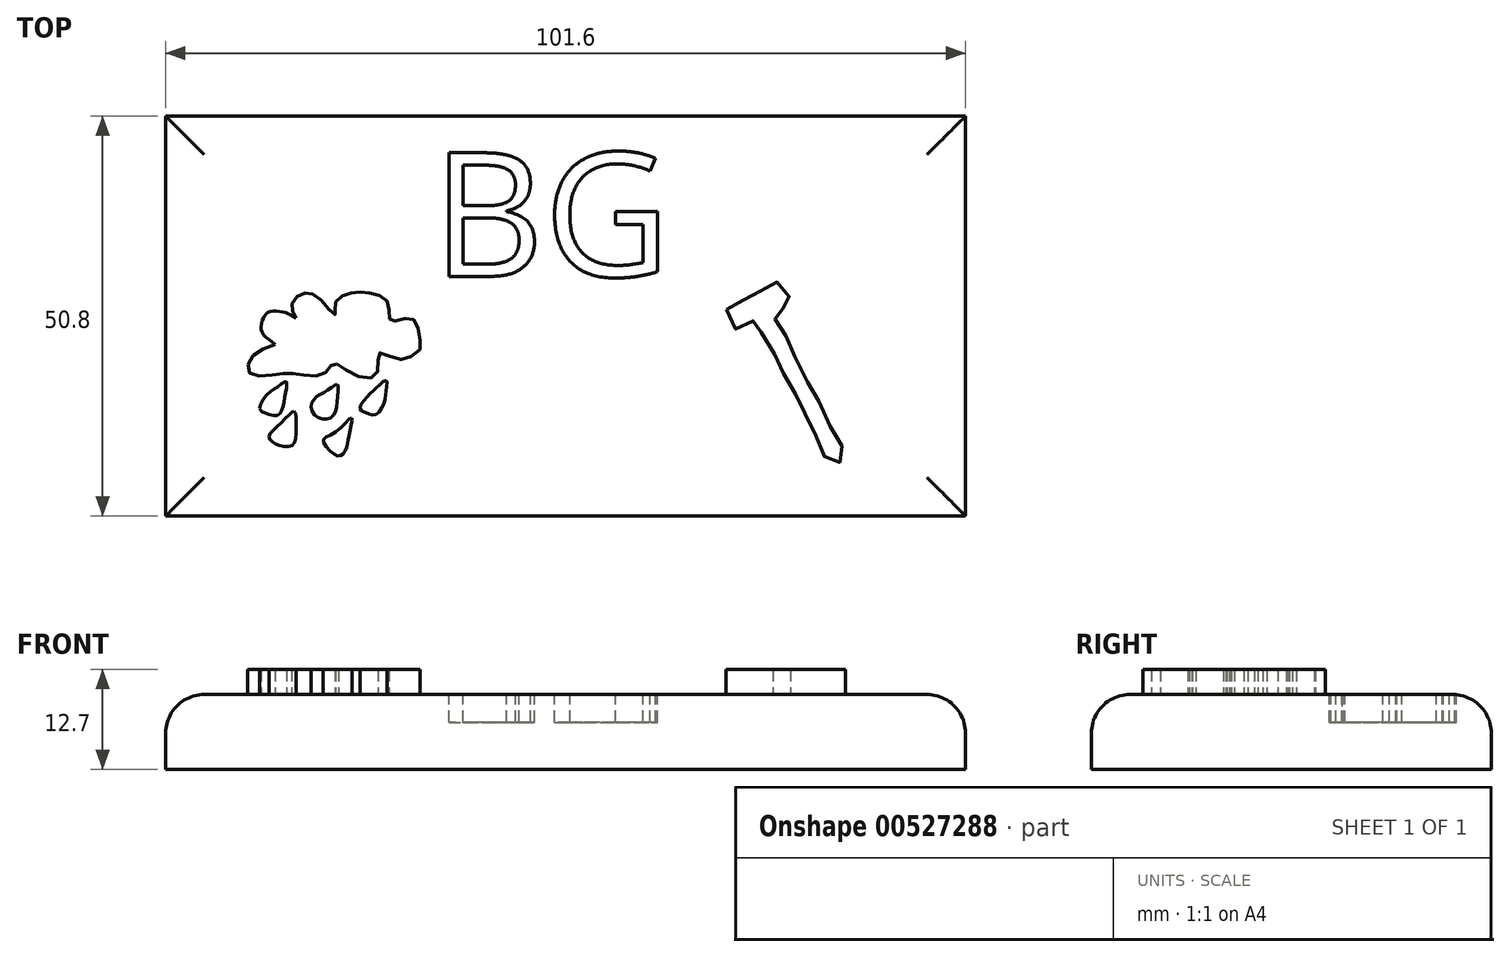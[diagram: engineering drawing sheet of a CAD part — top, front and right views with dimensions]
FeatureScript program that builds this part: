
annotation { "Feature Type Name" : "Feature", "Feature Type Description" : "" }
export const myFeature = defineFeature(function(context is Context, id is Id, definition is map)
    precondition{}
    {
        {
            var Q0;
            Q0=qCreatedBy(makeId("Top.planeOp"),FACE);
            var sketch = newSketch(context, id + "F0", { "sketchPlane" : qUnion([Q0])});
            skLineSegment(sketch, "E0.bottom", {"start": v(-46.77, 12.88) * mm, "end": v(54.83, 12.88) * mm});
            skLineSegment(sketch, "E0.top", {"start": v(-46.77, -37.92) * mm, "end": v(54.83, -37.92) * mm});
            skLineSegment(sketch, "E0.left", {"start": v(-46.77, 12.88) * mm, "end": v(-46.77, -37.92) * mm});
            skLineSegment(sketch, "E0.right", {"start": v(54.83, 12.88) * mm, "end": v(54.83, -37.92) * mm});
            skPoint(sketch, "E0.middle", {"position": v(4.03, -12.52) * mm});
            skSolve(sketch);
        }
        {
            var Q0;
            Q0=makeQuery(id+"F0.imprint","IMPRINT",FACE,{"disambiguationData":[TD([[makeQuery(id+"F0.imprint","IMPRINT",EDGE,{"derivedFrom":sQuery(id+"F0.wireOp",EDGE,"E0.bottom")}),-1.0]])]});
            extrude(context, id + "F1", {"entities" : qUnion([Q0]), "depth" : 9.52 * mm, "offsetDistance" : 25.4 * mm});
        }
        {
            var Q0;
            Q0=makeQuery(id+"F1.opExtrude","CAP_FACE",FACE,{"disambiguationData":[OSD([sQuery(id+"F0.wireOp",EDGE,"E0.bottom"),sQuery(id+"F0.wireOp",EDGE,"E0.top"),sQuery(id+"F0.wireOp",EDGE,"E0.left"),sQuery(id+"F0.wireOp",EDGE,"E0.right")])],"isStart":false});
            var sketch = newSketch(context, id + "F2", { "sketchPlane" : qUnion([Q0])});
            skText(sketch, "E1", { "text": "BG", "fontName": "OpenSans-Regular.ttf"});
            const initialGuessF2  = {"E1": [-0.01295, -0.00748, 1, 0, 0.01583]};
            skSetInitialGuess(sketch, initialGuessF2);
            skSolve(sketch);
        }
        {
            var Q0;
            Q0 = qSketchRegion(id + "F2", true);
            extrude(context, id + "F3", {"entities" : qUnion([Q0]), "operationType" : NewBodyOperationType.REMOVE, "oppositeDirection" : true, "depth" : 3.56 * mm, "offsetDistance" : 25.4 * mm});
        }
        {
            var Q0;
            Q0=makeQuery(id+"F1.opExtrude","CAP_EDGE",EDGE,{"disambiguationData":[OSD([sQuery(id+"F0.wireOp",EDGE,"E0.top")])],"isStart":false});
            var Q1;
            Q1=makeQuery(id+"F1.opExtrude","CAP_EDGE",EDGE,{"disambiguationData":[OSD([sQuery(id+"F0.wireOp",EDGE,"E0.left")])],"isStart":false});
            var Q2;
            Q2=makeQuery(id+"F1.opExtrude","CAP_EDGE",EDGE,{"disambiguationData":[OSD([sQuery(id+"F0.wireOp",EDGE,"E0.bottom")])],"isStart":false});
            var Q3;
            Q3=makeQuery(id+"F1.opExtrude","CAP_EDGE",EDGE,{"disambiguationData":[OSD([sQuery(id+"F0.wireOp",EDGE,"E0.right")])],"isStart":false});
            fillet(context, id + "F4", {"entities" : qUnion([Q0, Q1, Q2, Q3]), "radius" : 4.9 * mm, "tangentPropagation" : true, "allowEdgeOverflow" : false});
        }
        {
            var Q0;
            {var subQ0=sQuery(id+"F0.wireOp",EDGE,"E0.top");var subQ1=sQuery(id+"F0.wireOp",EDGE,"E0.right");var subQ2=sQuery(id+"F0.wireOp",EDGE,"E0.bottom");var subQ3=sQuery(id+"F0.wireOp",EDGE,"E0.left");Q0=makeQuery(id+"F3.boolean.opBoolean","SPLIT",FACE,{"disambiguationData":[TD([makeQuery(id+"F1.opExtrude","SWEPT_FACE",FACE,{"disambiguationData":[OSD([subQ2])]})])],"derivedFrom":makeQuery(id+"F1.opExtrude","CAP_FACE",FACE,{"disambiguationData":[OSD([subQ2,subQ0,subQ3,subQ1])],"isStart":false})});}
            var sketch = newSketch(context, id + "F5", { "sketchPlane" : qUnion([Q0])});
            skPoint(sketch, "E2.3.internal.snap0", {"position": v(-35.98, -19.88) * mm});
            skPoint(sketch, "E2.4.internal.snap0", {"position": v(-35.98, -19.88) * mm});
            skPoint(sketch, "E2.5.internal.snap0", {"position": v(-35.98, -19.88) * mm});
            skPoint(sketch, "E2.7.internal.snap0", {"position": v(-35.98, -19.88) * mm});
            skPoint(sketch, "E2.8.internal.snap0", {"position": v(-35.98, -19.88) * mm});
            skFitSpline(sketch, "E2", {"points": [v(-32.84, -16.11) * mm, v(-35.98, -17.92) * mm, v(-35.98, -19.88) * mm, v(-32.45, -19.88) * mm, v(-30, -19.88) * mm, v(-26.64, -19.88) * mm, v(-25.48, -18.56) * mm, v(-23.03, -19.88) * mm, v(-19.93, -19.88) * mm, v(-19.67, -17.27) * mm, v(-17.09, -18.05) * mm, v(-14.46, -16.76) * mm], "startDerivative": vector(-36.78, -13.1) * mm, "endDerivative": vector(25.49, 23.18) * mm});
            skPoint(sketch, "E3.6.internal.snap0", {"position": v(-25.22, -9.63) * mm});
            skPoint(sketch, "E3.7.internal.snap0", {"position": v(-25.22, -9.63) * mm});
            skFitSpline(sketch, "E3", {"points": [v(-14.46, -15.62) * mm, v(-15.65, -12.8) * mm, v(-18.14, -13.12) * mm, v(-18.47, -10.95) * mm, v(-20.64, -9.63) * mm, v(-23.35, -9.63) * mm, v(-25.22, -10.95) * mm, v(-25.22, -12.36) * mm, v(-27.15, -10.4) * mm, v(-29.22, -9.63) * mm, v(-30.74, -11.06) * mm, v(-30.2, -12.8) * mm], "startDerivative": vector(-5.04, 37.77) * mm, "endDerivative": vector(12.69, -21.45) * mm});
            skFitSpline(sketch, "E4", {"points": [v(-30.2, -12.8) * mm, v(-31.74, -12.03) * mm, v(-33.65, -12.03) * mm, v(-34.36, -12.8) * mm, v(-34.6, -14.41) * mm, v(-32.84, -16.11) * mm], "startDerivative": vector(-7.03, 4.53) * mm, "endDerivative": vector(9.72, -6.58) * mm});
            skFitSpline(sketch, "E5", {"points": [v(-34.84, -24.3) * mm, v(-34, -24.89) * mm, v(-32.57, -25.13) * mm, v(-31.98, -24.41) * mm, v(-31.62, -22.75) * mm, v(-31.38, -21.2) * mm, v(-31.5, -20.84) * mm, v(-32.45, -21.44) * mm, v(-33.76, -22.39) * mm, v(-34.84, -24.3) * mm]});
            skFitSpline(sketch, "E6", {"points": [v(-24.95, -21.2) * mm, v(-24.95, -22.98) * mm, v(-25.43, -25.13) * mm, v(-26.98, -25.6) * mm, v(-28.29, -24.3) * mm, v(-27.7, -22.87) * mm, v(-26.14, -21.91) * mm, v(-24.95, -21.2) * mm]});
            skFitSpline(sketch, "E7", {"points": [v(-22.1, -24.3) * mm, v(-21.14, -24.89) * mm, v(-20.07, -25) * mm, v(-19, -23.46) * mm, v(-18.76, -21.91) * mm, v(-18.76, -20.72) * mm, v(-19.93, -21.56) * mm, v(-21.02, -22.63) * mm, v(-22.1, -24.3) * mm]});
            skPoint(sketch, "E8.6.internal.snap0", {"position": v(-25.22, -30.14) * mm});
            skFitSpline(sketch, "E8", {"points": [v(-23.17, -25.48) * mm, v(-23.4, -27.27) * mm, v(-23.76, -29.06) * mm, v(-24.36, -30.14) * mm, v(-25.22, -30.14) * mm, v(-26.74, -28.34) * mm, v(-25.22, -27.27) * mm, v(-23.17, -25.48) * mm]});
            skFitSpline(sketch, "E9", {"points": [v(-30.43, -24.65) * mm, v(-30.2, -26.44) * mm, v(-30.67, -28.94) * mm, v(-32.7, -28.82) * mm, v(-33.65, -27.87) * mm, v(-32.1, -26.08) * mm, v(-30.43, -24.65) * mm]});
            skLineSegment(sketch, "E10", {"start": v(-14.46, -16.76) * mm, "end": v(-14.46, -15.62) * mm});
            skSolve(sketch);
        }
        {
            var Q0;
            Q0=makeQuery(id+"F5.imprint","IMPRINT",FACE,{"disambiguationData":[TD([[makeQuery(id+"F5.imprint","IMPRINT",EDGE,{"derivedFrom":sQuery(id+"F5.wireOp",EDGE,"E2")}),1.0]])]});
            var Q1;
            Q1=makeQuery(id+"F5.imprint","IMPRINT",FACE,{"disambiguationData":[TD([[makeQuery(id+"F5.imprint","IMPRINT",EDGE,{"derivedFrom":sQuery(id+"F5.wireOp",EDGE,"E7")}),1.0]])]});
            var Q2;
            Q2=makeQuery(id+"F5.imprint","IMPRINT",FACE,{"disambiguationData":[TD([[makeQuery(id+"F5.imprint","IMPRINT",EDGE,{"derivedFrom":sQuery(id+"F5.wireOp",EDGE,"E8")}),-1.0]])]});
            var Q3;
            Q3=makeQuery(id+"F5.imprint","IMPRINT",FACE,{"disambiguationData":[TD([[makeQuery(id+"F5.imprint","IMPRINT",EDGE,{"derivedFrom":sQuery(id+"F5.wireOp",EDGE,"E6")}),-1.0]])]});
            var Q4;
            Q4=makeQuery(id+"F5.imprint","IMPRINT",FACE,{"disambiguationData":[TD([[makeQuery(id+"F5.imprint","IMPRINT",EDGE,{"derivedFrom":sQuery(id+"F5.wireOp",EDGE,"E9")}),-1.0]])]});
            var Q5;
            Q5=makeQuery(id+"F5.imprint","IMPRINT",FACE,{"disambiguationData":[TD([[makeQuery(id+"F5.imprint","IMPRINT",EDGE,{"derivedFrom":sQuery(id+"F5.wireOp",EDGE,"E5")}),1.0]])]});
            extrude(context, id + "F6", {"entities" : qUnion([Q0, Q1, Q2, Q3, Q4, Q5]), "operationType" : NewBodyOperationType.ADD, "depth" : 3.17 * mm, "offsetDistance" : 25.4 * mm});
        }
        {
            var Q0;
            {var subQ0=sQuery(id+"F0.wireOp",EDGE,"E0.top");var subQ1=sQuery(id+"F0.wireOp",EDGE,"E0.right");var subQ2=sQuery(id+"F0.wireOp",EDGE,"E0.bottom");var subQ3=sQuery(id+"F0.wireOp",EDGE,"E0.left");Q0=makeQuery(id+"F3.boolean.opBoolean","SPLIT",FACE,{"disambiguationData":[TD([makeQuery(id+"F1.opExtrude","SWEPT_FACE",FACE,{"disambiguationData":[OSD([subQ2])]})])],"derivedFrom":makeQuery(id+"F1.opExtrude","CAP_FACE",FACE,{"disambiguationData":[OSD([subQ2,subQ0,subQ3,subQ1])],"isStart":false})});}
            var sketch = newSketch(context, id + "F7", { "sketchPlane" : qUnion([Q0])});
            skPoint(sketch, "E11.5.internal.snap0", {"position": v(32.01, -8.2) * mm});
            skPoint(sketch, "E11.7.internal.snap0", {"position": v(32.01, -8.2) * mm});
            skPoint(sketch, "E11.10.internal.snap0", {"position": v(32.01, -8.2) * mm});
            skFitSpline(sketch, "E11", {"points": [v(24.47, -11.67) * mm, v(25.93, -10.78) * mm, v(27.77, -9.83) * mm, v(29.34, -9.01) * mm, v(30.84, -8.2) * mm, v(32.01, -9.5) * mm, v(32.6, -10.44) * mm, v(32.01, -11.4) * mm, v(30.43, -12.08) * mm, v(31.04, -13.5) * mm, v(32.01, -15.08) * mm, v(33.02, -17.32) * mm, v(34.65, -20.73) * mm, v(35.95, -22.9) * mm, v(37.38, -25.97) * mm, v(38.8, -28.63) * mm, v(39.56, -29.92) * mm, v(38.4, -31.35) * mm, v(37.04, -30.6) * mm, v(36.22, -28.63) * mm, v(34.86, -25.7) * mm, v(33.83, -23.66) * mm, v(32.68, -21.4) * mm, v(31.31, -19.1) * mm, v(30.36, -16.98) * mm, v(28.73, -14.26) * mm, v(28.32, -13.03) * mm, v(26.68, -13.92) * mm, v(25.39, -14.05) * mm, v(24.47, -11.67) * mm]});
            skSolve(sketch);
        }
        {
            var Q0;
            Q0=makeQuery(id+"F7.imprint","IMPRINT",FACE,{"disambiguationData":[TD([[makeQuery(id+"F7.imprint","IMPRINT",EDGE,{"derivedFrom":sQuery(id+"F7.wireOp",EDGE,"E11")}),-1.0]])]});
            extrude(context, id + "F8", {"entities" : qUnion([Q0]), "operationType" : NewBodyOperationType.ADD, "depth" : 3.17 * mm, "offsetDistance" : 25.4 * mm});
        }
    });
